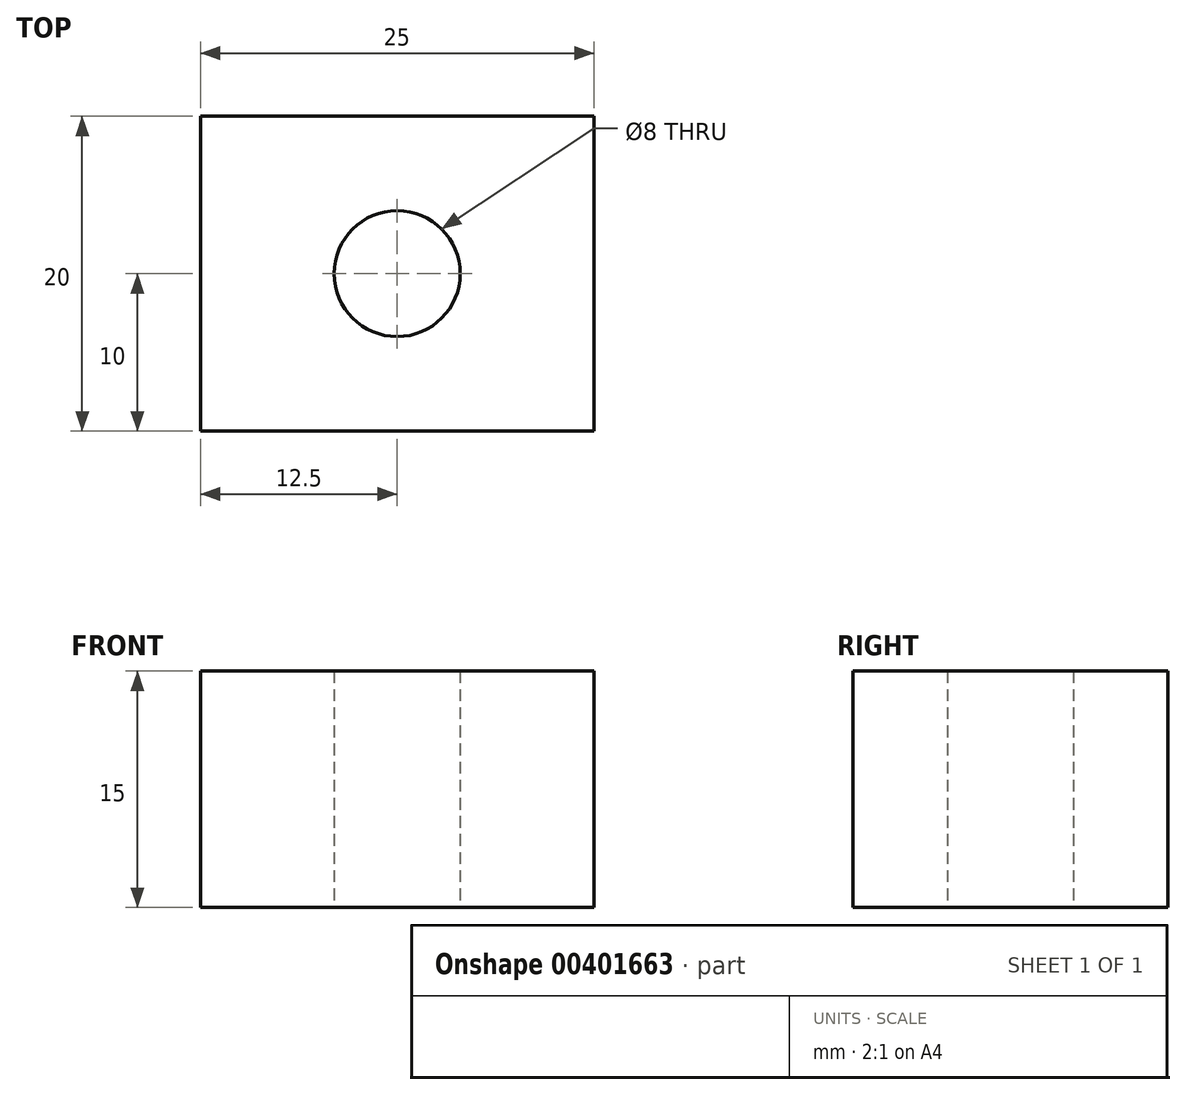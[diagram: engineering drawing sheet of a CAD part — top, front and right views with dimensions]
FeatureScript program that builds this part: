
annotation { "Feature Type Name" : "Feature", "Feature Type Description" : "" }
export const myFeature = defineFeature(function(context is Context, id is Id, definition is map)
    precondition{}
    {
        {
            var Q0;
            Q0=qCreatedBy(makeId("Top.planeOp"),FACE);
            var sketch = newSketch(context, id + "F0", { "sketchPlane" : qUnion([Q0])});
            skLineSegment(sketch, "E0.bottom", {"start": v(0, 0) * mm, "end": v(25, 0) * mm});
            skLineSegment(sketch, "E0.top", {"start": v(0, -20) * mm, "end": v(25, -20) * mm});
            skLineSegment(sketch, "E0.left", {"start": v(0, 0) * mm, "end": v(0, -20) * mm});
            skLineSegment(sketch, "E0.right", {"start": v(25, 0) * mm, "end": v(25, -20) * mm});
            skLineSegment(sketch, "E1", {"start": v(0, -10) * mm, "end": v(25, -10) * mm, "construction": true});
            skCircle(sketch, "E2", {"center": v(12.5, -10) * mm, "radius": 4 * mm});
            skSolve(sketch);
        }
        {
            var Q0;
            Q0=makeQuery(id+"F0.imprint","IMPRINT",FACE,{"disambiguationData":[TD([[makeQuery(id+"F0.imprint","IMPRINT",EDGE,{"derivedFrom":sQuery(id+"F0.wireOp",EDGE,"E0.bottom")}),-1.0]])]});
            extrude(context, id + "F1", {"entities" : qUnion([Q0]), "depth" : 15 * mm});
        }
    });
